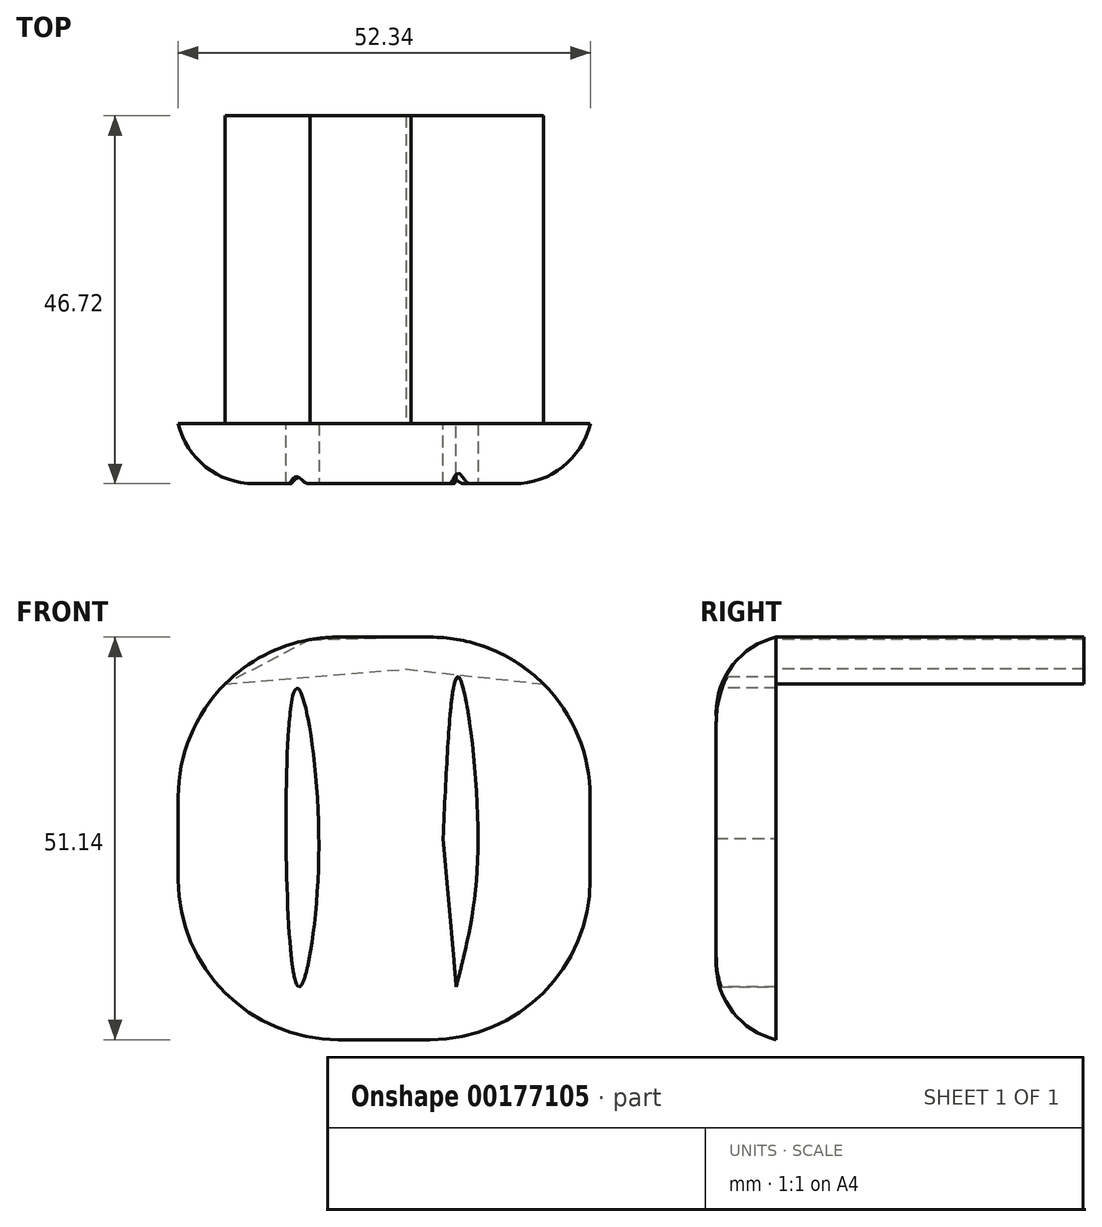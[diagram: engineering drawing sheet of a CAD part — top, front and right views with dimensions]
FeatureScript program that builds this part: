
annotation { "Feature Type Name" : "Feature", "Feature Type Description" : "" }
export const myFeature = defineFeature(function(context is Context, id is Id, definition is map)
    precondition{}
    {
        {
            var Q0;
            Q0=qCreatedBy(makeId("Front.planeOp"),FACE);
            var sketch = newSketch(context, id + "F0", { "sketchPlane" : qUnion([Q0])});
            skLineSegment(sketch, "E0.bottom", {"start": v(-5.85, -25.57) * mm, "end": v(5.85, -25.57) * mm});
            skLineSegment(sketch, "E0.top", {"start": v(-5.85, 25.57) * mm, "end": v(5.85, 25.57) * mm});
            skLineSegment(sketch, "E0.left", {"start": v(-26.17, -5.25) * mm, "end": v(-26.17, 5.25) * mm});
            skLineSegment(sketch, "E0.right", {"start": v(26.17, -5.25) * mm, "end": v(26.17, 5.25) * mm});
            skPoint(sketch, "E0.middle", {"position": v(0, 0) * mm});
            skPoint(sketch, "E1.visualSharp", {"position": v(-26.17, 25.57) * mm});
            skArc(sketch, "E1.filletArc", {"start": v(-5.85, 25.57) * mm, "mid": v(-20.22, 19.62) * mm, "end": v(-26.17, 5.25) * mm});
            skPoint(sketch, "E2.visualSharp", {"position": v(26.17, 25.57) * mm});
            skArc(sketch, "E2.filletArc", {"start": v(26.17, 5.25) * mm, "mid": v(20.22, 19.62) * mm, "end": v(5.85, 25.57) * mm});
            skPoint(sketch, "E3.visualSharp", {"position": v(26.17, -25.57) * mm});
            skArc(sketch, "E3.filletArc", {"start": v(5.85, -25.57) * mm, "mid": v(20.22, -19.62) * mm, "end": v(26.17, -5.25) * mm});
            skPoint(sketch, "E4.visualSharp", {"position": v(-26.17, -25.57) * mm});
            skArc(sketch, "E4.filletArc", {"start": v(-26.17, -5.25) * mm, "mid": v(-20.22, -19.62) * mm, "end": v(-5.85, -25.57) * mm});
            skSolve(sketch);
        }
        {
            var Q0;
            Q0=makeQuery(id+"F0.imprint","IMPRINT",FACE,{"disambiguationData":[TD([[makeQuery(id+"F0.imprint","IMPRINT",EDGE,{"derivedFrom":sQuery(id+"F0.wireOp",EDGE,"E0.bottom")}),1.0]])]});
            extrude(context, id + "F1", {"entities" : qUnion([Q0]), "depth" : 7.62 * mm});
        }
        {
            var Q0;
            Q0=makeQuery(id+"F1.opExtrude","CAP_FACE",FACE,{"disambiguationData":[OSD([sQuery(id+"F0.wireOp",EDGE,"E0.bottom"),sQuery(id+"F0.wireOp",EDGE,"E0.top"),sQuery(id+"F0.wireOp",EDGE,"E0.left"),sQuery(id+"F0.wireOp",EDGE,"E0.right"),sQuery(id+"F0.wireOp",EDGE,"E1.filletArc"),sQuery(id+"F0.wireOp",EDGE,"E2.filletArc"),sQuery(id+"F0.wireOp",EDGE,"E3.filletArc"),sQuery(id+"F0.wireOp",EDGE,"E4.filletArc")])],"isStart":false});
            fillet(context, id + "F2", {"entities" : qUnion([Q0]), "radius" : 9.9 * mm, "tangentPropagation" : true, "allowEdgeOverflow" : false});
        }
        {
            var Q0;
            Q0=makeQuery(id+"F1.opExtrude","CAP_FACE",FACE,{"disambiguationData":[OSD([sQuery(id+"F0.wireOp",EDGE,"E0.bottom"),sQuery(id+"F0.wireOp",EDGE,"E0.top"),sQuery(id+"F0.wireOp",EDGE,"E0.left"),sQuery(id+"F0.wireOp",EDGE,"E0.right"),sQuery(id+"F0.wireOp",EDGE,"E1.filletArc"),sQuery(id+"F0.wireOp",EDGE,"E2.filletArc"),sQuery(id+"F0.wireOp",EDGE,"E3.filletArc"),sQuery(id+"F0.wireOp",EDGE,"E4.filletArc")])],"isStart":true});
            var sketch = newSketch(context, id + "F3", { "sketchPlane" : qUnion([Q0])});
            skCircle(sketch, "E5", {"center": v(0, 0) * mm, "radius": 23.14 * mm});
            skSolve(sketch);
        }
        {
            var Q0;
            Q0=makeQuery(id+"F3.imprint","IMPRINT",FACE,{"disambiguationData":[TD([[makeQuery(id+"F3.imprint","IMPRINT",EDGE,{"derivedFrom":sQuery(id+"F3.wireOp",EDGE,"E5")}),1.0]])]});
            extrude(context, id + "F4", {"entities" : qUnion([Q0]), "operationType" : NewBodyOperationType.ADD, "oppositeDirection" : true, "depth" : 0.3 * mm});
        }
        {
            var Q0;
            Q0=makeQuery(id+"F1.opExtrude","CAP_FACE",FACE,{"disambiguationData":[OSD([sQuery(id+"F0.wireOp",EDGE,"E0.bottom"),sQuery(id+"F0.wireOp",EDGE,"E0.top"),sQuery(id+"F0.wireOp",EDGE,"E0.left"),sQuery(id+"F0.wireOp",EDGE,"E0.right"),sQuery(id+"F0.wireOp",EDGE,"E1.filletArc"),sQuery(id+"F0.wireOp",EDGE,"E2.filletArc"),sQuery(id+"F0.wireOp",EDGE,"E3.filletArc"),sQuery(id+"F0.wireOp",EDGE,"E4.filletArc")])],"isStart":true});
            var sketch = newSketch(context, id + "F5", { "sketchPlane" : qUnion([Q0])});
            skFitSpline(sketch, "E6", {"points": [v(-9.14, -18.84) * mm, v(-11.91, 0) * mm, v(-9.42, 20.5) * mm, v(-7.48, 0) * mm], "startDerivative": vector(-12.8, 49.42) * mm, "endDerivative": vector(4.23, -93.32) * mm});
            skFitSpline(sketch, "E7", {"points": [v(-9.14, -18.84) * mm, v(-7.48, 0) * mm], "startDerivative": vector(1.66, 18.84) * mm, "endDerivative": vector(1.66, 18.84) * mm});
            skFitSpline(sketch, "E8", {"points": [v(10.8, -18.84) * mm, v(8.31, 0) * mm, v(11.08, 19.12) * mm, v(12.47, 0) * mm, v(10.8, -18.84) * mm]});
            skSolve(sketch);
        }
        {
            var Q0;
            Q0 = qSketchRegion(id + "F5", true);
            extrude(context, id + "F6", {"entities" : qUnion([Q0]), "operationType" : NewBodyOperationType.REMOVE, "oppositeDirection" : true, "depth" : 25 * mm});
        }
        {
            var Q0;
            Q0=makeQuery(id+"F1.opExtrude","CAP_FACE",FACE,{"disambiguationData":[OSD([sQuery(id+"F0.wireOp",EDGE,"E0.bottom"),sQuery(id+"F0.wireOp",EDGE,"E0.top"),sQuery(id+"F0.wireOp",EDGE,"E0.left"),sQuery(id+"F0.wireOp",EDGE,"E0.right"),sQuery(id+"F0.wireOp",EDGE,"E1.filletArc"),sQuery(id+"F0.wireOp",EDGE,"E2.filletArc"),sQuery(id+"F0.wireOp",EDGE,"E3.filletArc"),sQuery(id+"F0.wireOp",EDGE,"E4.filletArc")])],"isStart":true});
            var sketch = newSketch(context, id + "F7", { "sketchPlane" : qUnion([Q0])});
            skFitSpline(sketch, "E9", {"points": [v(-20.22, 19.62) * mm, v(-12.49, 24.45) * mm, v(0, 25.57) * mm], "startDerivative": vector(15.34, 12.42) * mm, "endDerivative": vector(24.84, -0.18) * mm});
            skFitSpline(sketch, "E10", {"points": [v(9.43, 25.25) * mm, v(20.22, 19.62) * mm], "startDerivative": vector(10.79, -5.63) * mm, "endDerivative": vector(10.79, -5.63) * mm});
            skFitSpline(sketch, "E11", {"points": [v(9.43, 25.25) * mm, v(-4.47, 25.6) * mm], "startDerivative": vector(-13.9, 0.35) * mm, "endDerivative": vector(-13.9, 0.35) * mm});
            skFitSpline(sketch, "E12", {"points": [v(20.22, 19.62) * mm, v(-2.77, 21.5) * mm], "startDerivative": vector(-22.99, 1.88) * mm, "endDerivative": vector(-22.99, 1.88) * mm});
            skFitSpline(sketch, "E13", {"points": [v(-2.77, 21.5) * mm, v(-20.22, 19.62) * mm], "startDerivative": vector(-17.45, -1.88) * mm, "endDerivative": vector(-17.45, -1.88) * mm});
            skSolve(sketch);
        }
        {
            var Q0;
            Q0 = qSketchRegion(id + "F7", true);
            extrude(context, id + "F8", {"entities" : qUnion([Q0]), "operationType" : NewBodyOperationType.ADD, "depth" : 39.1 * mm});
        }
    });
